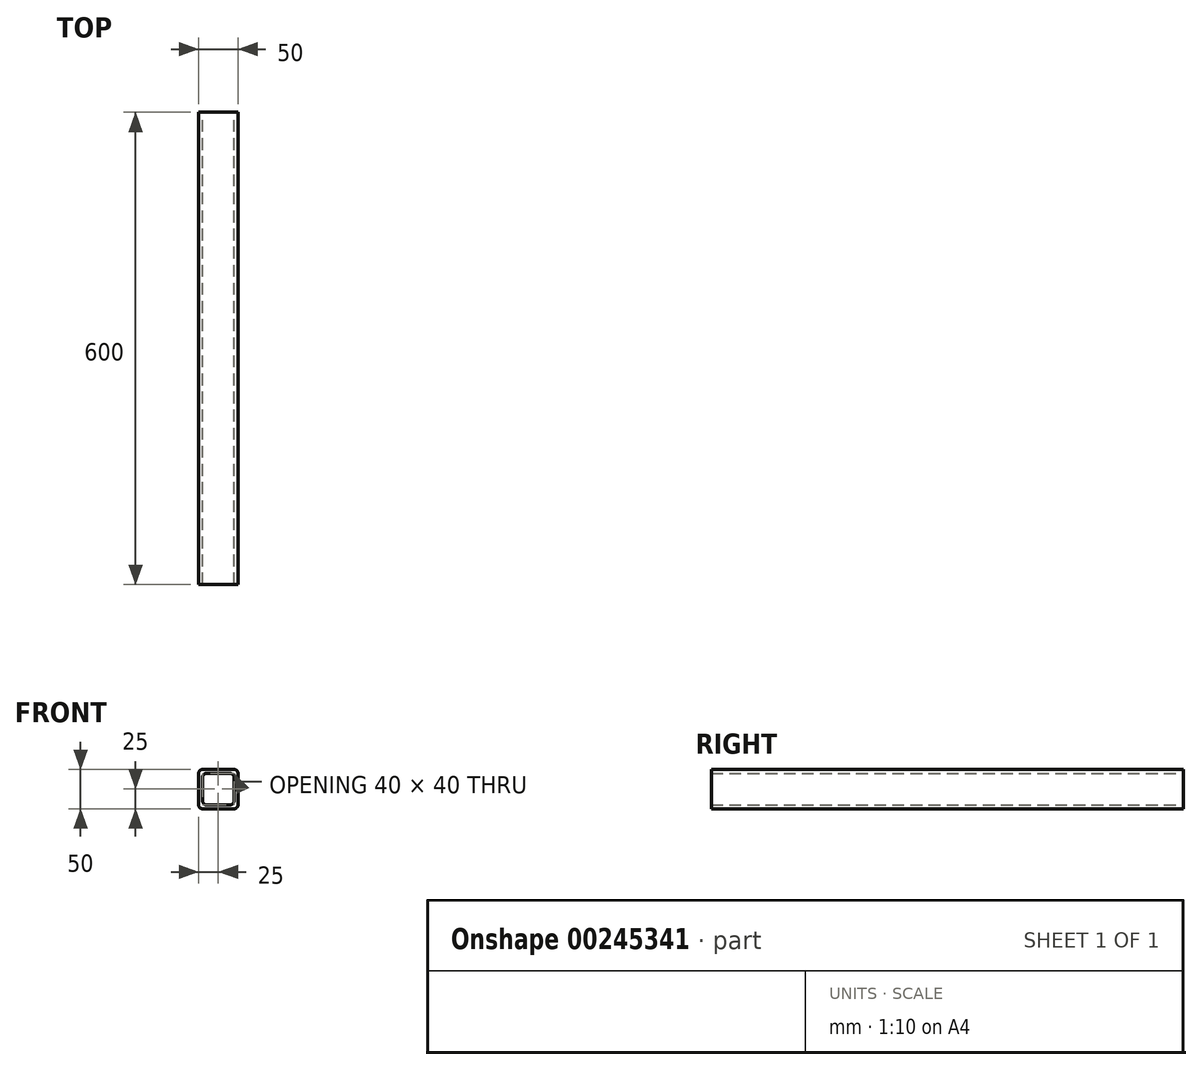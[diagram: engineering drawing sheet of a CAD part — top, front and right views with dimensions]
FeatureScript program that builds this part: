
annotation { "Feature Type Name" : "Feature", "Feature Type Description" : "" }
export const myFeature = defineFeature(function(context is Context, id is Id, definition is map)
    precondition{}
    {
        {
            var Q0;
            Q0=qCreatedBy(makeId("Front.planeOp"),FACE);
            var sketch = newSketch(context, id + "F0", { "sketchPlane" : qUnion([Q0])});
            skLineSegment(sketch, "E0.bottom", {"start": v(5, 0) * mm, "end": v(45, 0) * mm});
            skLineSegment(sketch, "E0.top", {"start": v(5, 50) * mm, "end": v(45, 50) * mm});
            skLineSegment(sketch, "E0.left", {"start": v(0, 5) * mm, "end": v(0, 45) * mm});
            skLineSegment(sketch, "E0.right", {"start": v(50, 5) * mm, "end": v(50, 45) * mm});
            skLineSegment(sketch, "E1.bottom", {"start": v(10, 45) * mm, "end": v(40, 45) * mm});
            skLineSegment(sketch, "E1.top", {"start": v(10, 5) * mm, "end": v(40, 5) * mm});
            skLineSegment(sketch, "E1.left", {"start": v(5, 40) * mm, "end": v(5, 10) * mm});
            skLineSegment(sketch, "E1.right", {"start": v(45, 40) * mm, "end": v(45, 10) * mm});
            skPoint(sketch, "E2.visualSharp", {"position": v(0, 50) * mm});
            skArc(sketch, "E2.filletArc", {"start": v(5, 50) * mm, "mid": v(1.46, 48.54) * mm, "end": v(0, 45) * mm});
            skPoint(sketch, "E3.visualSharp", {"position": v(50, 50) * mm});
            skArc(sketch, "E3.filletArc", {"start": v(50, 45) * mm, "mid": v(48.54, 48.54) * mm, "end": v(45, 50) * mm});
            skPoint(sketch, "E4.visualSharp", {"position": v(50, 0) * mm});
            skArc(sketch, "E4.filletArc", {"start": v(45, 0) * mm, "mid": v(48.54, 1.46) * mm, "end": v(50, 5) * mm});
            skPoint(sketch, "E5.visualSharp", {"position": v(0, 0) * mm});
            skArc(sketch, "E5.filletArc", {"start": v(0, 5) * mm, "mid": v(1.46, 1.46) * mm, "end": v(5, 0) * mm});
            skArc(sketch, "E6.filletArc", {"start": v(5, 10) * mm, "mid": v(6.46, 6.46) * mm, "end": v(10, 5) * mm});
            skArc(sketch, "E7.filletArc", {"start": v(10, 45) * mm, "mid": v(6.46, 43.54) * mm, "end": v(5, 40) * mm});
            skArc(sketch, "E8.filletArc", {"start": v(40, 5) * mm, "mid": v(43.54, 6.46) * mm, "end": v(45, 10) * mm});
            skArc(sketch, "E9.filletArc", {"start": v(45, 40) * mm, "mid": v(43.54, 43.54) * mm, "end": v(40, 45) * mm});
            skSolve(sketch);
        }
        {
            var Q0;
            Q0=makeQuery(id+"F0.imprint","IMPRINT",FACE,{"disambiguationData":[TD([[makeQuery(id+"F0.imprint","IMPRINT",EDGE,{"derivedFrom":sQuery(id+"F0.wireOp",EDGE,"E0.bottom")}),1.0]])]});
            extrude(context, id + "F1", {"entities" : qUnion([Q0]), "depth" : 600 * mm});
        }
    });
